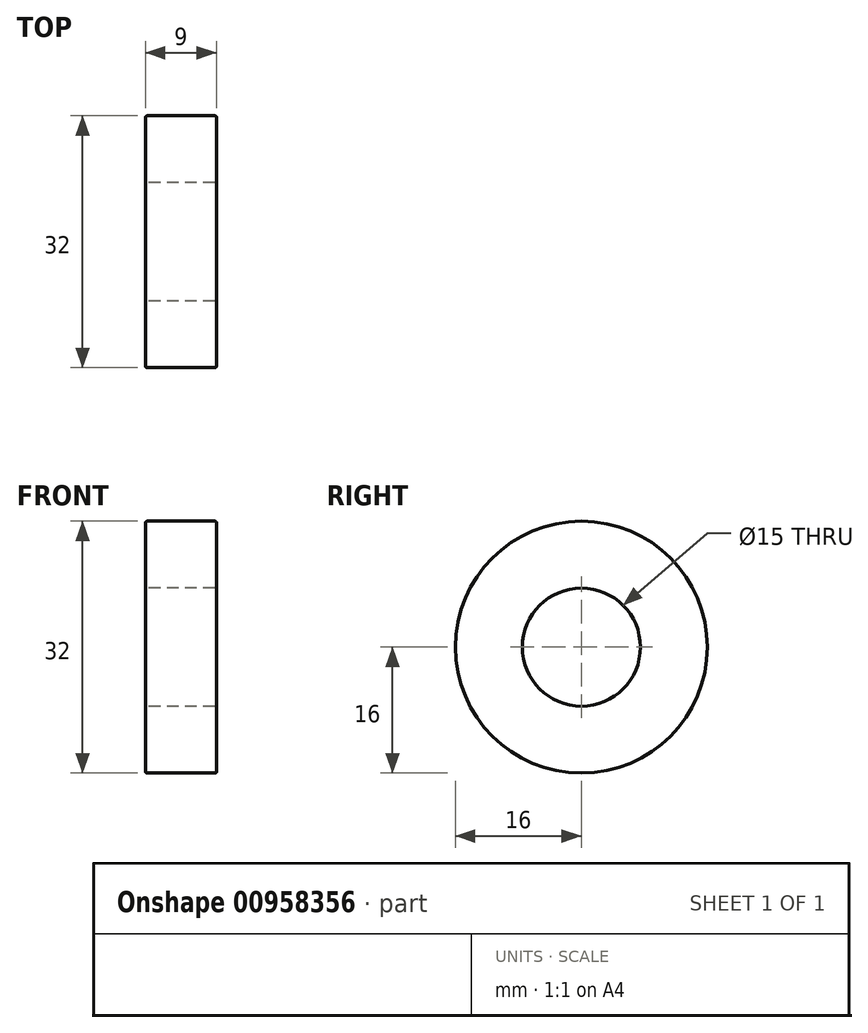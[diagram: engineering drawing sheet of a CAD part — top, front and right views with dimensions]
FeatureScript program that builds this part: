
annotation { "Feature Type Name" : "Feature", "Feature Type Description" : "" }
export const myFeature = defineFeature(function(context is Context, id is Id, definition is map)
    precondition{}
    {
        {
            var Q0;
            Q0=qCreatedBy(makeId("Front.planeOp"),FACE);
            var sketch = newSketch(context, id + "F0", { "sketchPlane" : qUnion([Q0])});
            skLineSegment(sketch, "E0.bottom", {"start": v(4.68, 16) * mm, "end": v(-4.32, 16) * mm});
            skLineSegment(sketch, "E0.top", {"start": v(4.68, 7.5) * mm, "end": v(-4.32, 7.5) * mm});
            skLineSegment(sketch, "E0.left", {"start": v(4.68, 16) * mm, "end": v(4.68, 7.5) * mm});
            skLineSegment(sketch, "E0.right", {"start": v(-4.32, 16) * mm, "end": v(-4.32, 7.5) * mm});
            skLineSegment(sketch, "E1", {"start": v(-4.3, 0) * mm, "end": v(5.95, 0) * mm});
            skSolve(sketch);
        }
        {
            var Q0;
            Q0 = qSketchRegion(id + "F0", true);
            var Q1;
            Q1=sQuery(id+"F0.wireOp",EDGE,"E1");
            revolve(context, id + "F1", {"surfaceOperationType" : NewSurfaceOperationType.NEW, "entities" : qUnion([Q0]), "axis" : qUnion([Q1]), "revolveType" : RevolveType.FULL});
        }
        {
            var Q0;
            Q0=makeQuery(id+"F1.opRevolve","SWEPT_FACE",FACE,{"disambiguationData":[OSD([sQuery(id+"F0.wireOp",EDGE,"E0.top")])]});
            var Q1;
            Q1=makeQuery(id+"F1.opRevolve","SWEPT_FACE",FACE,{"disambiguationData":[OSD([sQuery(id+"F0.wireOp",EDGE,"E0.bottom")])]});
            fillet(context, id + "F2", {"entities" : qUnion([Q0, Q1]), "radius" : 0.2 * mm, "tangentPropagation" : true, "allowEdgeOverflow" : false});
        }
    });
